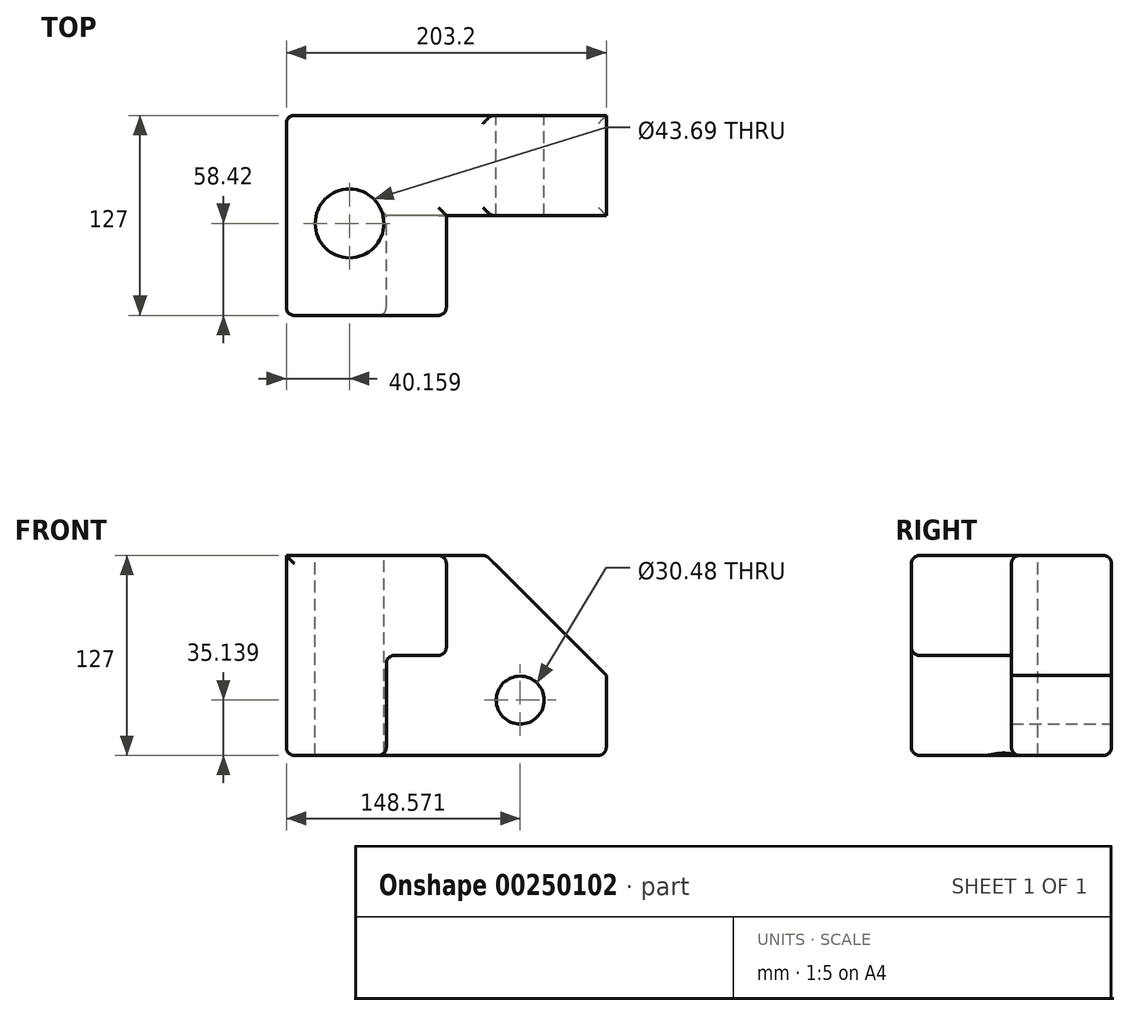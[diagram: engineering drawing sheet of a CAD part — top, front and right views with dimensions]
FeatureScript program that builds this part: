
annotation { "Feature Type Name" : "Feature", "Feature Type Description" : "" }
export const myFeature = defineFeature(function(context is Context, id is Id, definition is map)
    precondition{}
    {
        {
            var Q0;
            Q0=qCreatedBy(makeId("Front.planeOp"),FACE);
            var sketch = newSketch(context, id + "F0", { "sketchPlane" : qUnion([Q0])});
            skLineSegment(sketch, "E0.bottom", {"start": v(74.8, 63.5) * mm, "end": v(-128.4, 63.5) * mm});
            skLineSegment(sketch, "E0.top", {"start": v(74.8, -63.5) * mm, "end": v(-128.4, -63.5) * mm});
            skLineSegment(sketch, "E0.left", {"start": v(74.8, 63.5) * mm, "end": v(74.8, -63.5) * mm});
            skLineSegment(sketch, "E0.right", {"start": v(-128.4, 63.5) * mm, "end": v(-128.4, -63.5) * mm});
            skLineSegment(sketch, "E1", {"start": v(-26.8, 63.5) * mm, "end": v(-26.8, 0) * mm});
            skLineSegment(sketch, "E2", {"start": v(-26.8, 0) * mm, "end": v(-64.9, 0) * mm});
            skLineSegment(sketch, "E3", {"start": v(-64.9, 0) * mm, "end": v(-64.9, -63.5) * mm});
            skCircle(sketch, "E4", {"center": v(20.17, -28.36) * mm, "radius": 15.24 * mm});
            skSolve(sketch);
        }
        {
            var Q0;
            {var subQ1=sQuery(id+"F0.wireOp",EDGE,"E0.right");Q0=makeQuery(id+"F0.imprint","IMPRINT",FACE,{"disambiguationData":[TD([[makeQuery(id+"F0.imprint","IMPRINT",EDGE,{"derivedFrom":subQ1}),1.0]])]});}
            extrude(context, id + "F1", {"entities" : qUnion([Q0]), "depth" : 127 * mm});
        }
        {
            var Q0;
            {var subQ1=sQuery(id+"F0.wireOp",EDGE,"E0.left");Q0=makeQuery(id+"F0.imprint","IMPRINT",FACE,{"disambiguationData":[TD([[makeQuery(id+"F0.imprint","IMPRINT",EDGE,{"derivedFrom":subQ1}),-1.0]])]});}
            extrude(context, id + "F2", {"entities" : qUnion([Q0]), "operationType" : NewBodyOperationType.ADD, "depth" : 63.5 * mm});
        }
        {
            var Q0;
            Q0=makeQuery(id+"F2.opExtrude","SWEPT_EDGE",EDGE,{"disambiguationData":[OSD([sQuery(id+"F0.wireOp",EDGE,"E0.bottom"),sQuery(id+"F0.wireOp",EDGE,"E0.left")])]});
            chamfer(context, id + "F3", {"entities" : qUnion([Q0]), "width" : 76.2 * mm, "tangentPropagation" : true});
        }
        {
            var Q0;
            {var subQ0=sQuery(id+"F0.wireOp",EDGE,"E0.bottom");Q0=makeQuery(id+"F3.opChamfer","BLEND_EDGE",EDGE,{"blendedFrom":[makeQuery(id+"F2.opExtrude","SWEPT_EDGE",EDGE,{"disambiguationData":[OSD([subQ0,sQuery(id+"F0.wireOp",EDGE,"E0.left")])]}),makeQuery(id+"F2.boolean.opBoolean","MERGE",FACE,{"derivedFrom":[makeQuery(id+"F1.opExtrude","SWEPT_FACE",FACE,{"disambiguationData":[OSD([subQ0])]}),makeQuery(id+"F2.opExtrude","SWEPT_FACE",FACE,{"disambiguationData":[OSD([subQ0])]})]})],"blendedInto":[makeQuery(id+"F2.boolean.opBoolean","MERGE",FACE,{"derivedFrom":[makeQuery(id+"F1.opExtrude","SWEPT_FACE",FACE,{"disambiguationData":[OSD([subQ0])]}),makeQuery(id+"F2.opExtrude","SWEPT_FACE",FACE,{"disambiguationData":[OSD([subQ0])]})]})]});}
            var Q1;
            Q1=makeQuery(id+"F1.opExtrude","CAP_EDGE",EDGE,{"disambiguationData":[OSD([sQuery(id+"F0.wireOp",EDGE,"E0.right")])],"isStart":true});
            var Q2;
            Q2=makeQuery(id+"F2.opExtrude","CAP_EDGE",EDGE,{"disambiguationData":[OSD([sQuery(id+"F0.wireOp",EDGE,"E1")])],"isStart":false});
            var Q3;
            Q3=makeQuery(id+"F2.opExtrude","CAP_EDGE",EDGE,{"disambiguationData":[OSD([sQuery(id+"F0.wireOp",EDGE,"E2")])],"isStart":false});
            var Q4;
            Q4=makeQuery(id+"F1.opExtrude","SWEPT_EDGE",EDGE,{"disambiguationData":[OSD([sQuery(id+"F0.wireOp",EDGE,"E2"),sQuery(id+"F0.wireOp",EDGE,"E3")])]});
            var Q5;
            Q5=makeQuery(id+"F1.opExtrude","SWEPT_EDGE",EDGE,{"disambiguationData":[OSD([sQuery(id+"F0.wireOp",EDGE,"E0.bottom"),sQuery(id+"F0.wireOp",EDGE,"E1")])]});
            var Q6;
            Q6=makeQuery(id+"F2.opExtrude","CAP_EDGE",EDGE,{"disambiguationData":[OSD([sQuery(id+"F0.wireOp",EDGE,"E0.bottom")])],"isStart":false});
            var Q7;
            {var subQ0=sQuery(id+"F0.wireOp",EDGE,"E0.bottom");Q7=makeQuery(id+"F2.boolean.opBoolean","MERGE",EDGE,{"derivedFrom":[makeQuery(id+"F1.opExtrude","CAP_EDGE",EDGE,{"disambiguationData":[OSD([subQ0])],"isStart":true}),makeQuery(id+"F2.opExtrude","CAP_EDGE",EDGE,{"disambiguationData":[OSD([subQ0])],"isStart":true})]});}
            var Q8;
            Q8=makeQuery(id+"F1.opExtrude","CAP_EDGE",EDGE,{"disambiguationData":[OSD([sQuery(id+"F0.wireOp",EDGE,"E0.top")])],"isStart":false});
            var Q9;
            Q9=makeQuery(id+"F1.opExtrude","CAP_EDGE",EDGE,{"disambiguationData":[OSD([sQuery(id+"F0.wireOp",EDGE,"E0.right")])],"isStart":false});
            var Q10;
            Q10=makeQuery(id+"F1.opExtrude","CAP_EDGE",EDGE,{"disambiguationData":[OSD([sQuery(id+"F0.wireOp",EDGE,"E0.bottom")])],"isStart":false});
            var Q11;
            Q11=makeQuery(id+"F1.opExtrude","SWEPT_EDGE",EDGE,{"disambiguationData":[OSD([sQuery(id+"F0.wireOp",EDGE,"E0.top"),sQuery(id+"F0.wireOp",EDGE,"E3")])]});
            var Q12;
            Q12=makeQuery(id+"F1.opExtrude","CAP_EDGE",EDGE,{"disambiguationData":[OSD([sQuery(id+"F0.wireOp",EDGE,"E2")])],"isStart":false});
            var Q13;
            Q13=makeQuery(id+"F1.opExtrude","CAP_EDGE",EDGE,{"disambiguationData":[OSD([sQuery(id+"F0.wireOp",EDGE,"E3")])],"isStart":false});
            var Q14;
            Q14=makeQuery(id+"F2.opExtrude","CAP_EDGE",EDGE,{"disambiguationData":[OSD([sQuery(id+"F0.wireOp",EDGE,"E3")])],"isStart":false});
            var Q15;
            Q15=makeQuery(id+"F1.opExtrude","SWEPT_EDGE",EDGE,{"disambiguationData":[OSD([sQuery(id+"F0.wireOp",EDGE,"E0.top"),sQuery(id+"F0.wireOp",EDGE,"E0.right")])]});
            var Q16;
            Q16=makeQuery(id+"F1.opExtrude","CAP_EDGE",EDGE,{"disambiguationData":[OSD([sQuery(id+"F0.wireOp",EDGE,"E1")])],"isStart":false});
            var Q17;
            Q17=makeQuery(id+"F1.opExtrude","SWEPT_EDGE",EDGE,{"disambiguationData":[OSD([sQuery(id+"F0.wireOp",EDGE,"E1"),sQuery(id+"F0.wireOp",EDGE,"E2")])]});
            var Q18;
            {var subQ0=sQuery(id+"F0.wireOp",EDGE,"E0.top");Q18=makeQuery(id+"F2.boolean.opBoolean","MERGE",FACE,{"derivedFrom":[makeQuery(id+"F1.opExtrude","SWEPT_FACE",FACE,{"disambiguationData":[OSD([subQ0])]}),makeQuery(id+"F2.opExtrude","SWEPT_FACE",FACE,{"disambiguationData":[OSD([subQ0])]})]});}
            fillet(context, id + "F4", {"entities" : qUnion([Q0, Q1, Q2, Q3, Q4, Q5, Q6, Q7, Q8, Q9, Q10, Q11, Q12, Q13, Q14, Q15, Q16, Q17, Q18]), "radius" : 5.08 * mm, "tangentPropagation" : true, "allowEdgeOverflow" : false});
        }
        {
            var Q0;
            {var subQ0=sQuery(id+"F0.wireOp",EDGE,"E0.bottom");Q0=makeQuery(id+"F2.boolean.opBoolean","MERGE",FACE,{"derivedFrom":[makeQuery(id+"F1.opExtrude","SWEPT_FACE",FACE,{"disambiguationData":[OSD([subQ0])]}),makeQuery(id+"F2.opExtrude","SWEPT_FACE",FACE,{"disambiguationData":[OSD([subQ0])]})]});}
            var sketch = newSketch(context, id + "F5", { "sketchPlane" : qUnion([Q0])});
            skCircle(sketch, "E5", {"center": v(-88.24, -68.58) * mm, "radius": 21.85 * mm});
            skSolve(sketch);
        }
        {
            var Q0;
            Q0=makeQuery(id+"F5.imprint","IMPRINT",FACE,{"disambiguationData":[TD([[makeQuery(id+"F5.imprint","IMPRINT",EDGE,{"derivedFrom":sQuery(id+"F5.wireOp",EDGE,"E5")}),1.0]])]});
            extrude(context, id + "F6", {"entities" : qUnion([Q0]), "operationType" : NewBodyOperationType.REMOVE, "oppositeDirection" : true, "depth" : 228.6 * mm});
        }
    });
